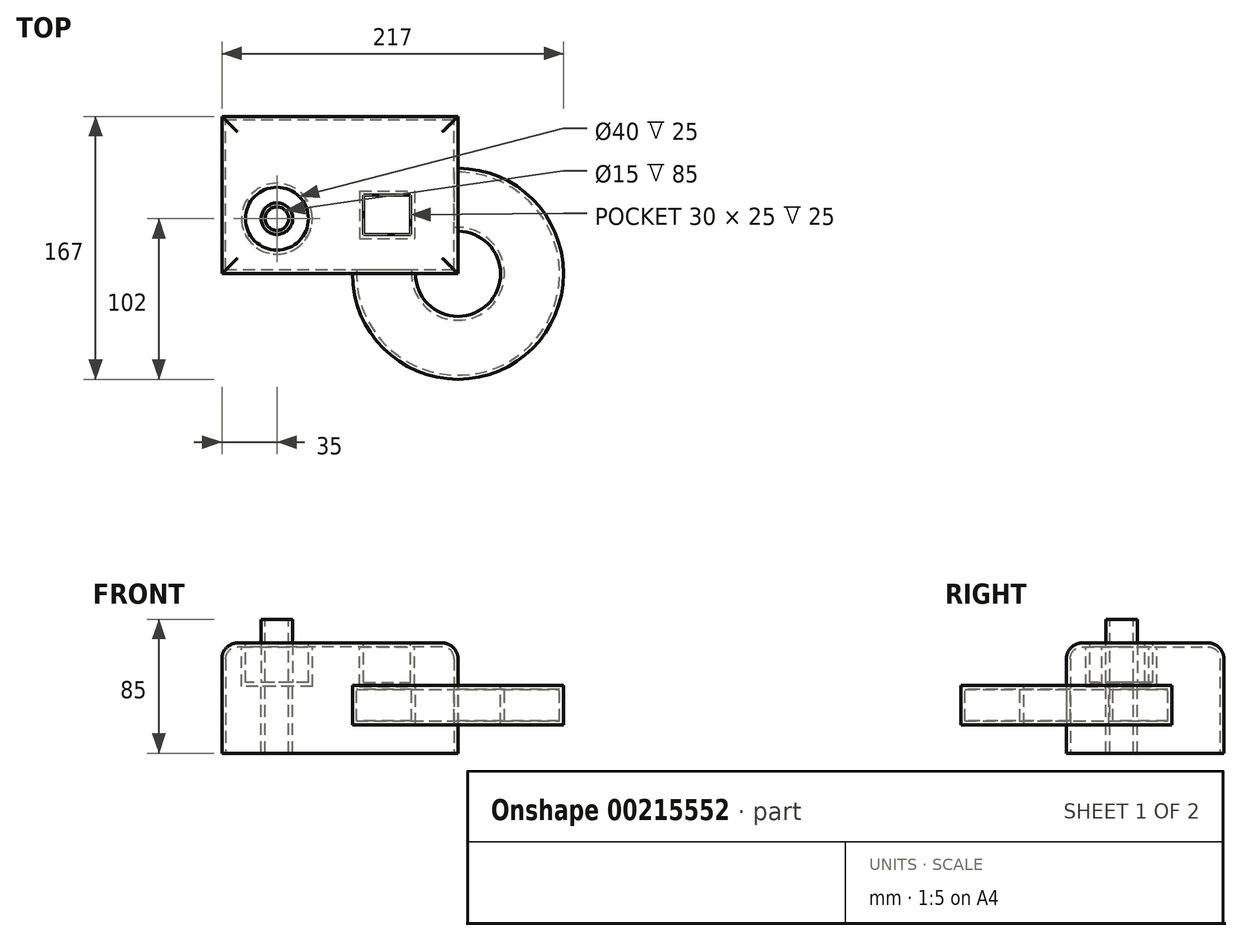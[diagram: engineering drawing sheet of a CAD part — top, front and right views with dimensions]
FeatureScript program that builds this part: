
annotation { "Feature Type Name" : "Feature", "Feature Type Description" : "" }
export const myFeature = defineFeature(function(context is Context, id is Id, definition is map)
    precondition{}
    {
        {
            var Q0;
            Q0=qCreatedBy(makeId("Front.planeOp"),FACE);
            var sketch = newSketch(context, id + "F0", { "sketchPlane" : qUnion([Q0])});
            skLineSegment(sketch, "E0.bottom", {"start": v(75, 35) * mm, "end": v(-75, 35) * mm});
            skLineSegment(sketch, "E0.top", {"start": v(75, -35) * mm, "end": v(-75, -35) * mm});
            skLineSegment(sketch, "E0.left", {"start": v(75, 35) * mm, "end": v(75, -35) * mm});
            skLineSegment(sketch, "E0.right", {"start": v(-75, 35) * mm, "end": v(-75, -35) * mm});
            skPoint(sketch, "E0.middle", {"position": v(0, 0) * mm});
            skSolve(sketch);
        }
        {
            var Q0;
            Q0 = qSketchRegion(id + "F0", true);
            extrude(context, id + "F1", {"entities" : qUnion([Q0]), "endBound" : BoundingType.SYMMETRIC, "depth" : 100 * mm});
        }
        {
            var Q0;
            Q0=makeQuery(id+"F1.opExtrude","SWEPT_FACE",FACE,{"disambiguationData":[OSD([sQuery(id+"F0.wireOp",EDGE,"E0.bottom")])]});
            var sketch = newSketch(context, id + "F2", { "sketchPlane" : qUnion([Q0])});
            skCircle(sketch, "E1", {"center": v(-40, -15) * mm, "radius": 20 * mm});
            skSolve(sketch);
        }
        {
            var Q0;
            Q0 = qSketchRegion(id + "F2", true);
            extrude(context, id + "F3", {"entities" : qUnion([Q0]), "operationType" : NewBodyOperationType.REMOVE, "oppositeDirection" : true, "depth" : 25 * mm});
        }
        {
            var Q0;
            Q0=makeQuery(id+"F3.boolean.opBoolean","COPY",FACE,{"derivedFrom":makeQuery(id+"F3.opExtrude","CAP_FACE",FACE,{"disambiguationData":[OSD([sQuery(id+"F2.wireOp",EDGE,"E1")])],"isStart":false})});
            var sketch = newSketch(context, id + "F4", { "sketchPlane" : qUnion([Q0])});
            skCircle(sketch, "E2", {"center": v(-40, -15) * mm, "radius": 10 * mm});
            skSolve(sketch);
        }
        {
            var Q0;
            Q0 = qSketchRegion(id + "F4", true);
            extrude(context, id + "F5", {"entities" : qUnion([Q0]), "operationType" : NewBodyOperationType.ADD, "depth" : 40 * mm});
        }
        {
            var Q0;
            Q0=makeQuery(id+"F1.opExtrude","SWEPT_EDGE",EDGE,{"disambiguationData":[OSD([sQuery(id+"F0.wireOp",EDGE,"E0.bottom"),sQuery(id+"F0.wireOp",EDGE,"E0.right")])]});
            var Q1;
            Q1=makeQuery(id+"F1.opExtrude","CAP_EDGE",EDGE,{"disambiguationData":[OSD([sQuery(id+"F0.wireOp",EDGE,"E0.bottom")])],"isStart":false});
            var Q2;
            Q2=makeQuery(id+"F1.opExtrude","SWEPT_EDGE",EDGE,{"disambiguationData":[OSD([sQuery(id+"F0.wireOp",EDGE,"E0.bottom"),sQuery(id+"F0.wireOp",EDGE,"E0.left")])]});
            var Q3;
            Q3=makeQuery(id+"F1.opExtrude","CAP_EDGE",EDGE,{"disambiguationData":[OSD([sQuery(id+"F0.wireOp",EDGE,"E0.bottom")])],"isStart":true});
            fillet(context, id + "F6", {"entities" : qUnion([Q0, Q1, Q2, Q3]), "radius" : 10 * mm, "tangentPropagation" : true, "allowEdgeOverflow" : false});
        }
        {
            var Q0;
            Q0=makeQuery(id+"F1.opExtrude","SWEPT_FACE",FACE,{"disambiguationData":[OSD([sQuery(id+"F0.wireOp",EDGE,"E0.left")])]});
            var sketch = newSketch(context, id + "F7", { "sketchPlane" : qUnion([Q0])});
            skLineSegment(sketch, "E3.bottom", {"start": v(-23, 8) * mm, "end": v(17, 8) * mm});
            skLineSegment(sketch, "E3.top", {"start": v(-23, -17) * mm, "end": v(17, -17) * mm});
            skLineSegment(sketch, "E3.left", {"start": v(-23, 8) * mm, "end": v(-23, -17) * mm});
            skLineSegment(sketch, "E3.right", {"start": v(17, 8) * mm, "end": v(17, -17) * mm});
            skSolve(sketch);
        }
        {
            var Q0;
            Q0 = qSketchRegion(id + "F7", true);
            var Q1;
            Q1=makeQuery(id+"F1.opExtrude","CAP_EDGE",EDGE,{"disambiguationData":[OSD([sQuery(id+"F0.wireOp",EDGE,"E0.left")])],"isStart":false});
            revolve(context, id + "F8", {"operationType" : NewBodyOperationType.ADD, "entities" : qUnion([Q0]), "axis" : qUnion([Q1]), "revolveType" : RevolveType.FULL});
        }
        {
            var Q0;
            Q0=makeQuery(id+"F5.opExtrude","CAP_FACE",FACE,{"disambiguationData":[OSD([sQuery(id+"F4.wireOp",EDGE,"E2")])],"isStart":false});
            var sketch = newSketch(context, id + "F9", { "sketchPlane" : qUnion([Q0])});
            skLineSegment(sketch, "E4", {"start": v(-40, -15) * mm, "end": v(-40, -5) * mm});
            skSolve(sketch);
        }
        {
            var Q0;
            Q0=sQuery(id+"F9.wireOp",VERTEX,"E4.start");
            var Q1;
            Q1=makeQuery(id+"F1.opExtrude","SWEPT_BODY",BODY,{"disambiguationData":[OSD([sQuery(id+"F0.wireOp",EDGE,"E0.bottom"),sQuery(id+"F0.wireOp",EDGE,"E0.top"),sQuery(id+"F0.wireOp",EDGE,"E0.left"),sQuery(id+"F0.wireOp",EDGE,"E0.right")])]});
            hole(context, id + "F10", {"style" : HoleStyle.SIMPLE, "endStyle" : HoleEndStyle.THROUGH, "holeDiameter" : 15 * mm, "locations" : qUnion([Q0]), "scope" : qUnion([Q1]), "isTappedThrough" : true});
        }
        {
            var Q0;
            Q0=makeQuery(id+"F1.opExtrude","SWEPT_FACE",FACE,{"disambiguationData":[OSD([sQuery(id+"F0.wireOp",EDGE,"E0.bottom")])]});
            var sketch = newSketch(context, id + "F11", { "sketchPlane" : qUnion([Q0])});
            skLineSegment(sketch, "E5.bottom", {"start": v(15, 0) * mm, "end": v(45, 0) * mm});
            skLineSegment(sketch, "E5.top", {"start": v(15, -25) * mm, "end": v(45, -25) * mm});
            skLineSegment(sketch, "E5.left", {"start": v(15, 0) * mm, "end": v(15, -25) * mm});
            skLineSegment(sketch, "E5.right", {"start": v(45, 0) * mm, "end": v(45, -25) * mm});
            skSolve(sketch);
        }
        {
            var Q0;
            Q0 = qSketchRegion(id + "F11", true);
            extrude(context, id + "F12", {"entities" : qUnion([Q0]), "operationType" : NewBodyOperationType.REMOVE, "oppositeDirection" : true, "depth" : 25 * mm});
        }
        {
            var Q0;
            Q0=makeQuery(id+"F1.opExtrude","SWEPT_FACE",FACE,{"disambiguationData":[OSD([sQuery(id+"F0.wireOp",EDGE,"E0.top")])]});
            shell(context, id + "F13", {"entities" : qUnion([Q0]), "thickness" : 2.5 * mm});
        }
    });
